# Revit family: Panneau passe-fils
name_source: partatom
category: Equipement spécialisé
units: mm (PartAtom-declared; Revit-internal decimal feet)

## family parameters
Basée sur le plan de construction = Non
Cote de connecteur circulaire = Utiliser le diamètre
Couper avec des vides une fois chargée = Non
Partagée = Oui
Point de calcul de pièce = Non
Toujours verticalement = Oui
Type d'élément = Normal

## types (1)
- Accessoires d'enveloppes Legrand
    Classe d'application = EC000322
    Couleur = IDS_NOIR
    EAN = 3245060465223
    Elévation par défaut = 0 mm  [stored 0 ft]
    Fonction = Guide câble
    Largeur (mm) = 482 mm  [stored 1.58136 ft]
    Libellé BIM = Accessoires d'enveloppes Legrand
    Lien e-catalogue = https://www.legrand.fr
    Longueur = 385
    Matière = Métal
    Modèle = Panneau de brassage
    Nombre d'unités en hauteur = 1
    Profondeur (mm) = 90 mm  [stored 0.295276 ft]
    RAL = 9005
    Référence Legrand = 046522

note: [stored X ft] marks values corroborated as IEEE doubles in the binary element streams (Revit-internal decimal feet)
